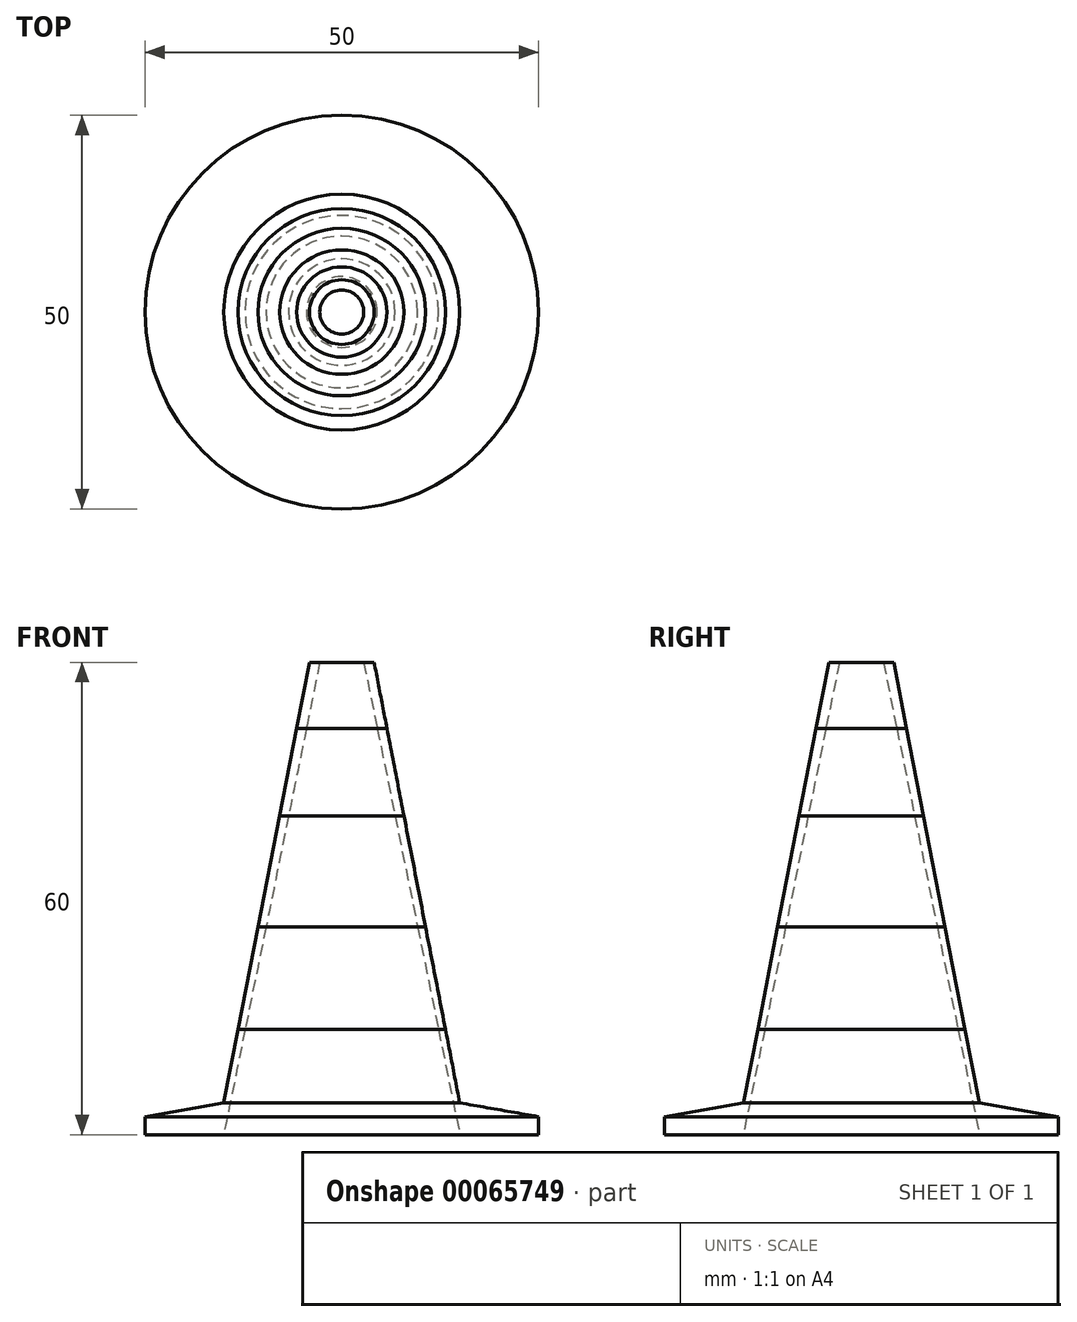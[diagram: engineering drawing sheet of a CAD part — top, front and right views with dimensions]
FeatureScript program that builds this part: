
annotation { "Feature Type Name" : "Feature", "Feature Type Description" : "" }
export const myFeature = defineFeature(function(context is Context, id is Id, definition is map)
    precondition{}
    {
        {
            var Q0;
            Q0=qCreatedBy(makeId("Front.planeOp"),FACE);
            var sketch = newSketch(context, id + "F0", { "sketchPlane" : qUnion([Q0])});
            skLineSegment(sketch, "E0", {"start": v(0, 0) * mm, "end": v(-25, 0) * mm});
            skLineSegment(sketch, "E1", {"start": v(-25, 0) * mm, "end": v(-25, 2.28) * mm});
            skLineSegment(sketch, "E2", {"start": v(-25, 2.28) * mm, "end": v(-14.98, 4.05) * mm});
            skLineSegment(sketch, "E3", {"start": v(-14.98, 4.05) * mm, "end": v(-4.1, 60) * mm});
            skLineSegment(sketch, "E4", {"start": v(-4.1, 60) * mm, "end": v(0, 60) * mm});
            skLineSegment(sketch, "E5", {"start": v(0, 60) * mm, "end": v(0, 0) * mm});
            skLineSegment(sketch, "E6", {"start": v(-13.17, 13.4) * mm, "end": v(0, 13.4) * mm});
            skLineSegment(sketch, "E7", {"start": v(-10.64, 26.4) * mm, "end": v(0, 26.4) * mm});
            skLineSegment(sketch, "E8", {"start": v(-7.9, 40.5) * mm, "end": v(0, 40.5) * mm});
            skLineSegment(sketch, "E9", {"start": v(-5.74, 51.6) * mm, "end": v(0, 51.6) * mm});
            skSolve(sketch);
        }
        {
            var Q0;
            {var subQ0=sQuery(id+"F0.wireOp",EDGE,"E4");Q0=makeQuery(id+"F0.imprint","IMPRINT",FACE,{"disambiguationData":[TD([[makeQuery(id+"F0.imprint","IMPRINT",EDGE,{"derivedFrom":subQ0}),-1.0]])]});}
            var Q1;
            Q1=sQuery(id+"F0.wireOp",EDGE,"E5");
            revolve(context, id + "F1", {"entities" : qUnion([Q0]), "axis" : qUnion([Q1]), "revolveType" : RevolveType.FULL});
        }
        {
            var Q0;
            {var subQ0=sQuery(id+"F0.wireOp",EDGE,"E8");Q0=makeQuery(id+"F0.imprint","IMPRINT",FACE,{"disambiguationData":[TD([[makeQuery(id+"F0.imprint","IMPRINT",EDGE,{"derivedFrom":subQ0}),1.0]])]});}
            var Q1;
            Q1=sQuery(id+"F0.wireOp",EDGE,"E5");
            revolve(context, id + "F2", {"entities" : qUnion([Q0]), "axis" : qUnion([Q1]), "revolveType" : RevolveType.FULL});
        }
        {
            var Q0;
            {var subQ0=sQuery(id+"F0.wireOp",EDGE,"E7");Q0=makeQuery(id+"F0.imprint","IMPRINT",FACE,{"disambiguationData":[TD([[makeQuery(id+"F0.imprint","IMPRINT",EDGE,{"derivedFrom":subQ0}),1.0]])]});}
            var Q1;
            Q1=sQuery(id+"F0.wireOp",EDGE,"E5");
            revolve(context, id + "F3", {"entities" : qUnion([Q0]), "axis" : qUnion([Q1]), "revolveType" : RevolveType.FULL});
        }
        {
            var Q0;
            {var subQ0=sQuery(id+"F0.wireOp",EDGE,"E6");Q0=makeQuery(id+"F0.imprint","IMPRINT",FACE,{"disambiguationData":[TD([[makeQuery(id+"F0.imprint","IMPRINT",EDGE,{"derivedFrom":subQ0}),1.0]])]});}
            var Q1;
            Q1=sQuery(id+"F0.wireOp",EDGE,"E5");
            revolve(context, id + "F4", {"entities" : qUnion([Q0]), "axis" : qUnion([Q1]), "revolveType" : RevolveType.FULL});
        }
        {
            var Q0;
            {var subQ3=sQuery(id+"F0.wireOp",EDGE,"E0");Q0=makeQuery(id+"F0.imprint","IMPRINT",FACE,{"disambiguationData":[TD([[makeQuery(id+"F0.imprint","IMPRINT",EDGE,{"derivedFrom":subQ3}),-1.0]])]});}
            var Q1;
            Q1=sQuery(id+"F0.wireOp",EDGE,"E5");
            revolve(context, id + "F5", {"entities" : qUnion([Q0]), "axis" : qUnion([Q1]), "revolveType" : RevolveType.FULL});
        }
        {
            var Q0;
            Q0=makeQuery(id+"F5.opRevolve","SWEPT_FACE",FACE,{"disambiguationData":[OSD([sQuery(id+"F0.wireOp",EDGE,"E0")])]});
            var sketch = newSketch(context, id + "F6", { "sketchPlane" : qUnion([Q0])});
            skCircle(sketch, "E10", {"center": v(0, 0) * mm, "radius": 15 * mm});
            skSolve(sketch);
        }
        {
            var Q0;
            Q0=makeQuery(id+"F6.imprint","IMPRINT",FACE,{"disambiguationData":[TD([[makeQuery(id+"F6.imprint","IMPRINT",EDGE,{"derivedFrom":sQuery(id+"F6.wireOp",EDGE,"E10")}),1.0]])]});
            extrude(context, id + "F7", {"entities" : qUnion([Q0]), "operationType" : NewBodyOperationType.REMOVE, "endBound" : BoundingType.THROUGH_ALL, "oppositeDirection" : true, "depth" : 25 * mm, "hasDraft" : true, "draftAngle" : 11.5 * degree, "draftPullDirection" : true});
        }
    });
